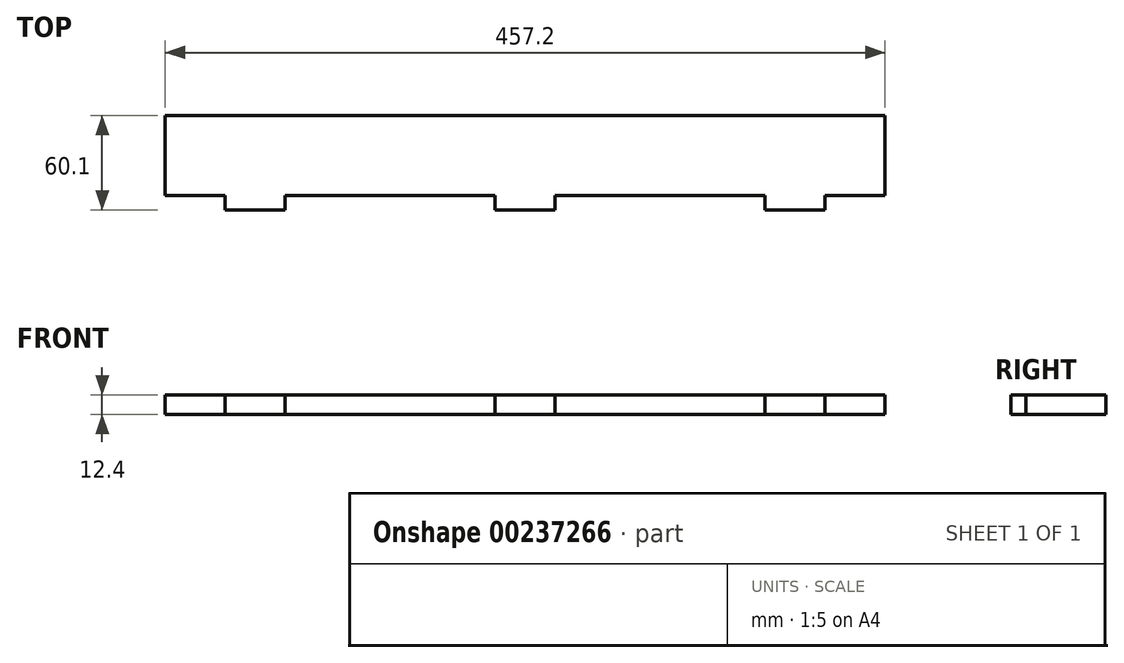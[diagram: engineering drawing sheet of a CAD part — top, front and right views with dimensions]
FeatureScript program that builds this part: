
annotation { "Feature Type Name" : "Feature", "Feature Type Description" : "" }
export const myFeature = defineFeature(function(context is Context, id is Id, definition is map)
    precondition{}
    {
        {
            var Q0;
            Q0=qCreatedBy(makeId("Top.planeOp"),FACE);
            var sketch = newSketch(context, id + "F0", { "sketchPlane" : qUnion([Q0])});
            skLineSegment(sketch, "E0.bottom", {"start": v(-72.59, -3.28) * mm, "end": v(384.61, -3.28) * mm});
            skLineSegment(sketch, "E0.top", {"start": v(-72.59, 47.52) * mm, "end": v(384.61, 47.52) * mm});
            skLineSegment(sketch, "E0.left", {"start": v(-72.59, -3.28) * mm, "end": v(-72.59, 47.52) * mm});
            skLineSegment(sketch, "E0.right", {"start": v(384.61, -3.28) * mm, "end": v(384.61, 47.52) * mm});
            skSolve(sketch);
        }
        {
            var Q0;
            Q0=makeQuery(id+"F0.imprint","IMPRINT",FACE,{"disambiguationData":[TD([[makeQuery(id+"F0.imprint","IMPRINT",EDGE,{"derivedFrom":sQuery(id+"F0.wireOp",EDGE,"E0.bottom")}),1.0]])]});
            extrude(context, id + "F1", {"entities" : qUnion([Q0]), "depth" : 12.4 * mm});
        }
        {
            var Q0;
            Q0=makeQuery(id+"F1.opExtrude","SWEPT_FACE",FACE,{"disambiguationData":[OSD([sQuery(id+"F0.wireOp",EDGE,"E0.bottom")])]});
            var sketch = newSketch(context, id + "F2", { "sketchPlane" : qUnion([Q0])});
            skLineSegment(sketch, "E1.bottom", {"start": v(-34.49, 12.4) * mm, "end": v(3.61, 12.4) * mm});
            skLineSegment(sketch, "E1.top", {"start": v(-34.49, 0) * mm, "end": v(3.61, 0) * mm});
            skLineSegment(sketch, "E1.left", {"start": v(-34.49, 12.4) * mm, "end": v(-34.49, 0) * mm});
            skLineSegment(sketch, "E1.right", {"start": v(3.61, 12.4) * mm, "end": v(3.61, 0) * mm});
            skLineSegment(sketch, "E2.bottom", {"start": v(136.96, 12.4) * mm, "end": v(175.06, 12.4) * mm});
            skLineSegment(sketch, "E2.top", {"start": v(136.96, 0) * mm, "end": v(175.06, 0) * mm});
            skLineSegment(sketch, "E2.left", {"start": v(136.96, 12.4) * mm, "end": v(136.96, 0) * mm});
            skLineSegment(sketch, "E2.right", {"start": v(175.06, 12.4) * mm, "end": v(175.06, 0) * mm});
            skLineSegment(sketch, "E3.bottom", {"start": v(346.51, 12.4) * mm, "end": v(308.41, 12.4) * mm});
            skLineSegment(sketch, "E3.top", {"start": v(346.51, 0) * mm, "end": v(308.41, 0) * mm});
            skLineSegment(sketch, "E3.left", {"start": v(346.51, 12.4) * mm, "end": v(346.51, 0) * mm});
            skLineSegment(sketch, "E3.right", {"start": v(308.41, 12.4) * mm, "end": v(308.41, 0) * mm});
            skSolve(sketch);
        }
        {
            var Q0;
            Q0=makeQuery(id+"F2.imprint","IMPRINT",FACE,{"disambiguationData":[TD([[makeQuery(id+"F2.imprint","IMPRINT",EDGE,{"derivedFrom":sQuery(id+"F2.wireOp",EDGE,"E1.bottom")}),-1.0]])]});
            var Q1;
            Q1=makeQuery(id+"F2.imprint","IMPRINT",FACE,{"disambiguationData":[TD([[makeQuery(id+"F2.imprint","IMPRINT",EDGE,{"derivedFrom":sQuery(id+"F2.wireOp",EDGE,"E2.bottom")}),-1.0]])]});
            var Q2;
            Q2=makeQuery(id+"F2.imprint","IMPRINT",FACE,{"disambiguationData":[TD([[makeQuery(id+"F2.imprint","IMPRINT",EDGE,{"derivedFrom":sQuery(id+"F2.wireOp",EDGE,"E3.bottom")}),-1.0]])]});
            extrude(context, id + "F3", {"entities" : qUnion([Q0, Q1, Q2]), "operationType" : NewBodyOperationType.ADD, "depth" : 9.3 * mm});
        }
    });
